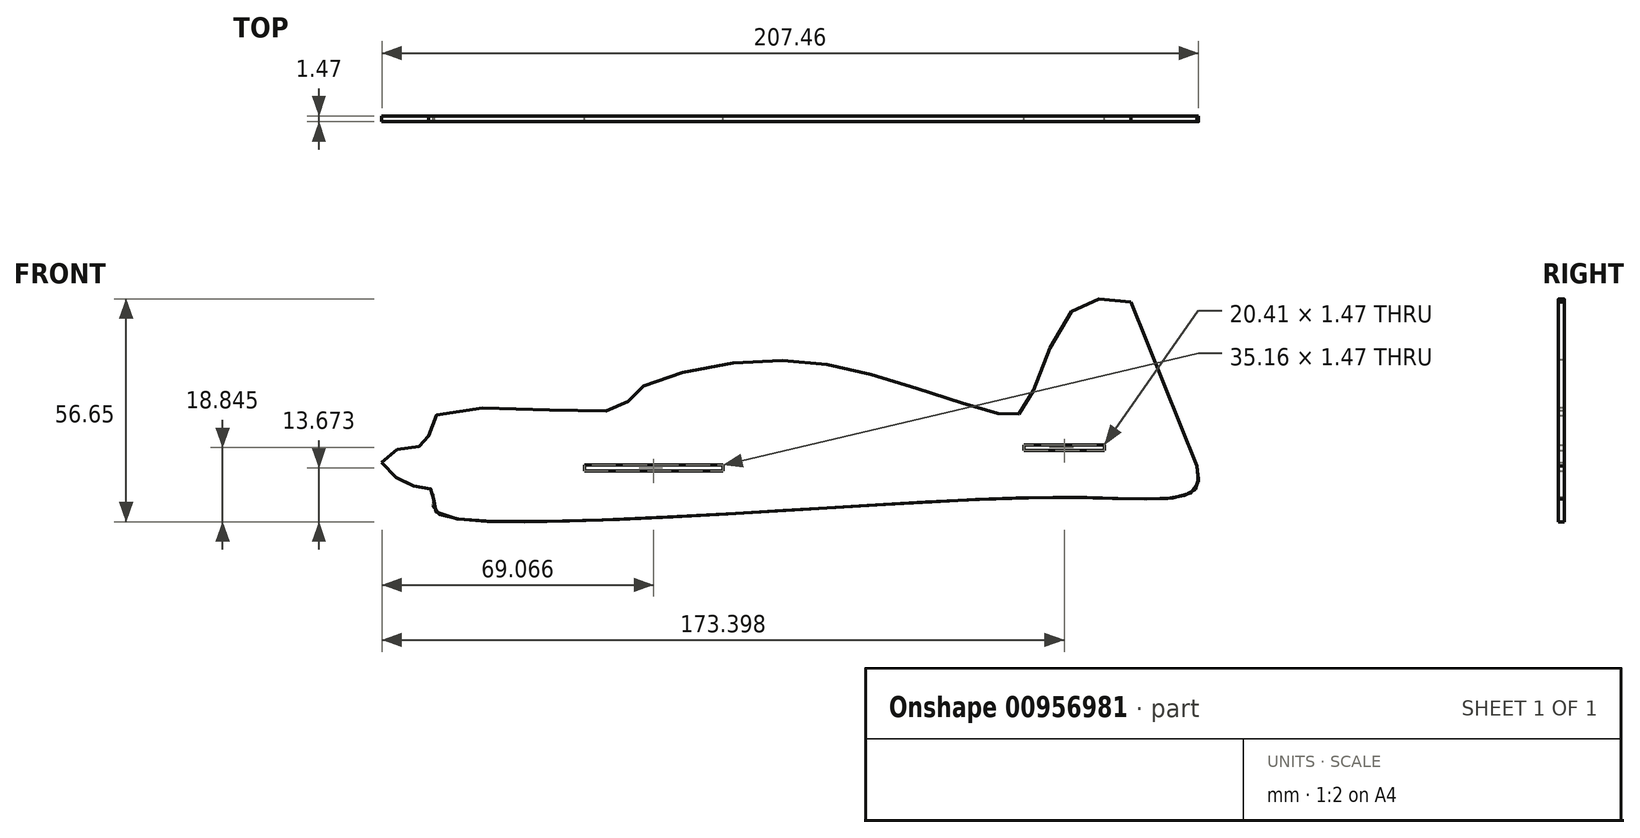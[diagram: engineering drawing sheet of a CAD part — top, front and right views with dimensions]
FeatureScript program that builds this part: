
annotation { "Feature Type Name" : "Feature", "Feature Type Description" : "" }
export const myFeature = defineFeature(function(context is Context, id is Id, definition is map)
    precondition{}
    {
        {
            var Q0;
            Q0=qCreatedBy(makeId("Front.planeOp"),FACE);
            var sketch = newSketch(context, id + "F0", { "sketchPlane" : qUnion([Q0])});
            skLineSegment(sketch, "E0.bottom", {"start": v(-114.3, 50.8) * mm, "end": v(114.3, 50.8) * mm, "construction": true});
            skLineSegment(sketch, "E0.top", {"start": v(-114.3, -50.8) * mm, "end": v(114.3, -50.8) * mm, "construction": true});
            skLineSegment(sketch, "E0.left", {"start": v(-114.3, 50.8) * mm, "end": v(-114.3, -50.8) * mm, "construction": true});
            skLineSegment(sketch, "E0.right", {"start": v(114.3, 50.8) * mm, "end": v(114.3, -50.8) * mm, "construction": true});
            skPoint(sketch, "E0.middle", {"position": v(0, 0) * mm});
            skFitSpline(sketch, "E1", {"points": [v(-109.81, 3.14) * mm, v(-104.44, 6.82) * mm, v(-98.22, 7.95) * mm, v(-96.52, 14.73) * mm, v(-49.58, 16.71) * mm, v(-45.9, 20.67) * mm, v(-15.64, 28.87) * mm, v(18.3, 24.35) * mm, v(47.71, 15.3) * mm, v(53.37, 16.71) * mm, v(65.53, 41.6) * mm, v(80.52, 43.86) * mm], "startDerivative": vector(81.3, 85.59) * mm, "endDerivative": vector(189.83, -32.41) * mm});
            skLineSegment(sketch, "E2", {"start": v(80.52, 43.86) * mm, "end": v(97.26, 2.16) * mm});
            skFitSpline(sketch, "E3", {"points": [v(97.26, 2.16) * mm, v(97.26, -3.08) * mm, v(92.09, -5.8) * mm, v(67.62, -5.8) * mm, v(2.4, -8.51) * mm, v(-84.85, -11.77) * mm, v(-96.8, -8.24) * mm, v(-96.65, -4.12) * mm, v(-102.58, -2.7) * mm, v(-109.81, 3.14) * mm], "startDerivative": vector(16.83, -96.68) * mm, "endDerivative": vector(-80.51, 93.55) * mm});
            skLineSegment(sketch, "E4.bottom", {"start": v(-23.16, 2.42) * mm, "end": v(-58.33, 2.42) * mm});
            skLineSegment(sketch, "E4.top", {"start": v(-23.16, 0.95) * mm, "end": v(-58.33, 0.95) * mm});
            skLineSegment(sketch, "E4.left", {"start": v(-23.16, 2.42) * mm, "end": v(-23.16, 0.95) * mm});
            skLineSegment(sketch, "E4.right", {"start": v(-58.33, 2.42) * mm, "end": v(-58.33, 0.95) * mm});
            skPoint(sketch, "E4.middle", {"position": v(-40.74, 1.68) * mm});
            skLineSegment(sketch, "E5.bottom", {"start": v(73.8, 7.6) * mm, "end": v(53.38, 7.6) * mm});
            skLineSegment(sketch, "E5.top", {"start": v(73.8, 6.12) * mm, "end": v(53.38, 6.12) * mm});
            skLineSegment(sketch, "E5.left", {"start": v(73.8, 7.6) * mm, "end": v(73.8, 6.12) * mm});
            skLineSegment(sketch, "E5.right", {"start": v(53.38, 7.6) * mm, "end": v(53.38, 6.12) * mm});
            skPoint(sketch, "E5.middle", {"position": v(63.59, 6.85) * mm});
            skSolve(sketch);
        }
        {
            var Q0;
            Q0=makeQuery(id+"F0.imprint","IMPRINT",FACE,{"disambiguationData":[TD([[makeQuery(id+"F0.imprint","IMPRINT",EDGE,{"derivedFrom":sQuery(id+"F0.wireOp",EDGE,"E1")}),-1.0]])]});
            extrude(context, id + "F1", {"entities" : qUnion([Q0]), "depth" : 1.47 * mm, "offsetDistance" : 25.4 * mm});
        }
    });
